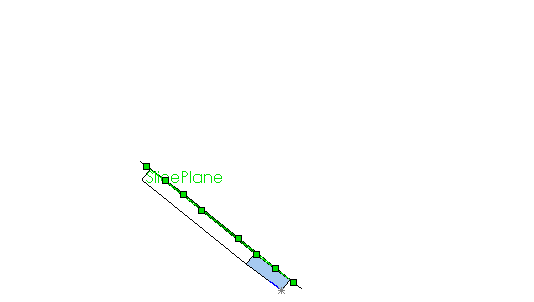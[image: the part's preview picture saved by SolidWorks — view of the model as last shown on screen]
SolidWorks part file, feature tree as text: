
SOLIDWORKS PART (.sldprt)
format: sldprt  version: not decoded by parser v0  size: 200,704 bytes
history: native  units: mm
features: sketch x4, cut_extrude x2, extrude x1, plane x1 (+12 scaffold rows collapsed)
feature tree (20):
  scaffold x12  (default folders/planes/origin — collapsed)
  sketch  "Sketch1"  dims[c1.D3=6.35mm c1.D4=6.35mm c1.D12=6.35mm c1.D15=6.35mm c2.D4=6.35mm c2.D3=6.35mm c2.D7=6.35mm c2.D10=6.35mm c2.D1=31.75mm c2.D2=19.05mm c3.D3=~13.171213mm c3.D5=9.525mm c3.D6=12.7mm c3.D7=15.875mm c3.D8=0.254mm c3.D9=0.254mm c3.D10=~12.710176mm c3.D11=19.05mm c3.D13=7.9375mm c4.D6=15.875mm c4.D14=15.875mm c5.D6=~3.96875mm c5.D11=6.35mm c6.D6=~23.422007mm c6.D4=12.7mm c7.D6=19.05mm c7.D11=7.62mm c7.D12=4.318mm c7.D13=4.318mm]
  extrude  "Extrude1"  Depth=66.04mm
  sketch  "Sketch2"  dims[c1.D4=3.9624mm c1.D5=3.9624mm c1.D6=3.9624mm c1.D1=25.4mm c1.D2=9.525mm c1.D3=~4.777706mm c1.D7=25.4mm c2.D2=9.525mm]
  cut_extrude  "Cut-Extrude1"  Depth=63.5mm
  sketch  "Sketch4"  dims[D4=3.9624mm D5=3.9624mm D1=9.525mm D2=38.1mm D3=12.7mm]
  cut_extrude  "Cut-Extrude3"  Depth=7.62mm
  plane  "SlicePlane"  Offset=2.8194mm
  sketch  "Sketch5"
decode coverage: 6 of 7 modeling features carry decoded parameters
note: ~ marks probable driven/reference dimensions
note: suppression state not decoded; provenance and decode notes live in map.json
